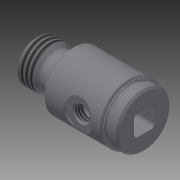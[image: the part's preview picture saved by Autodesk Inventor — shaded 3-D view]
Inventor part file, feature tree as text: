
AUTODESK INVENTOR PART (.ipt)
format: ipt  version: 2013 (Build 170138000, 138)  size: 262,656 bytes
history: native  units: in
note: dims shown in document units (in); Inventor stores cm internally (conversion verified against a paired STEP export)
features: other x119, sketch x5, revolve x4, thread x2, extrude x1
ambient origin geometry x8: Origin, YZ Plane, XZ Plane, XY Plane, X Axis, Y Axis, Z Axis, Center Point
bodies: Solid1 (feature_tree)
feature tree (131):
  revolve  "Revolution1"  [1 undecoded]
  thread  "Thread1"  [1 undecoded]
  revolve  "Revolution2"  [1 undecoded]
  revolve  "Revolution3"  [1 undecoded]
  thread  "Thread2"  [1 undecoded]
  revolve  "Revolution4"  [1 undecoded]
  extrude  "Extrusion1"  [1 undecoded]
  other  "m1_XY"
  other  "m1_YZ"
  other  "m1_ZX"
  other  "m1_X"
  other  "m1_Y"
  other  "m1_Z"
  other  "m1_Center"
  other  "m2_XY"
  other  "m2_YZ"
  other  "m2_ZX"
  other  "m2_X"
  other  "m2_Y"
  other  "m2_Z"
  other  "m2_Center"
  other  "s1_XY"
  other  "s1_YZ"
  other  "s1_ZX"
  other  "s1_X"
  other  "s1_Y"
  other  "s1_Z"
  other  "s1_Center"
  other  "s2_XY"
  other  "s2_YZ"
  other  "s2_ZX"
  other  "s2_X"
  other  "s2_Y"
  other  "s2_Z"
  other  "s2_Center"
  other  "dp1_XY"
  other  "dp1_YZ"
  other  "dp1_ZX"
  other  "dp1_X"
  other  "dp1_Y"
  other  "dp1_Z"
  other  "dp1_Center"
  other  "dp2_XY"
  other  "dp2_YZ"
  other  "dp2_ZX"
  other  "dp2_X"
  other  "dp2_Y"
  other  "dp2_Z"
  other  "dp2_Center"
  other  "rod_guide_XY"
  other  "rod_guide_YZ"
  other  "rod_guide_ZX"
  other  "rod_guide_X"
  other  "rod_guide_Y"
  other  "rod_guide_Z"
  other  "rod_guide_Center"
  other  "to_tube_XY"
  other  "to_tube_YZ"
  other  "to_tube_ZX"
  other  "to_tube_X"
  other  "to_tube_Y"
  other  "to_tube_Z"
  other  "to_tube_Center"
  other  "to_foot_bracket_XY"
  other  "to_foot_bracket_YZ"
  other  "to_foot_bracket_ZX"
  other  "to_foot_bracket_X"
  other  "to_foot_bracket_Y"
  other  "to_foot_bracket_Z"
  other  "to_foot_bracket_Center"
  other  "to_nut_XY"
  other  "to_nut_YZ"
  other  "to_nut_ZX"
  other  "to_nut_X"
  other  "to_nut_Y"
  other  "to_nut_Z"
  other  "to_nut_Center"
  other  "to_trunnion_brackets_XY"
  other  "to_trunnion_brackets_YZ"
  other  "to_trunnion_brackets_ZX"
  other  "to_trunnion_brackets_X"
  other  "to_trunnion_brackets_Y"
  other  "to_trunnion_brackets_Z"
  other  "to_trunnion_brackets_Center"
  other  "to_trunnion_brackets1_XY"
  other  "to_trunnion_brackets1_YZ"
  other  "to_trunnion_brackets1_ZX"
  other  "to_trunnion_brackets1_X"
  other  "to_trunnion_brackets1_Y"
  other  "to_trunnion_brackets1_Z"
  other  "to_trunnion_brackets1_Center"
  other  "to_trunnion_brackets2_XY"
  other  "to_trunnion_brackets2_YZ"
  other  "to_trunnion_brackets2_ZX"
  other  "to_trunnion_brackets2_X"
  other  "to_trunnion_brackets2_Y"
  other  "to_trunnion_brackets2_Z"
  other  "to_trunnion_brackets2_Center"
  other  "t1_XY"
  other  "t1_YZ"
  other  "t1_ZX"
  other  "t1_X"
  other  "t1_Y"
  other  "t1_Z"
  other  "t1_Center"
  other  "port_XY"
  other  "port_YZ"
  other  "port_ZX"
  other  "port_X"
  other  "port_Y"
  other  "port_Z"
  other  "port_Center"
  other  "rod_guide_1_XY"
  other  "rod_guide_1_YZ"
  other  "rod_guide_1_ZX"
  other  "rod_guide_1_X"
  other  "rod_guide_1_Y"
  other  "rod_guide_1_Z"
  other  "rod_guide_1_Center"
  other  "rod_guide_11_XY"
  other  "rod_guide_11_YZ"
  other  "rod_guide_11_ZX"
  other  "rod_guide_11_X"
  other  "rod_guide_11_Y"
  other  "rod_guide_11_Z"
  other  "rod_guide_11_Center"
  sketch  "Sketch_2"  dims[d0=360.0deg d1=0.1537in d2=0.0in d3=360.0deg]
  sketch  "Sketch_3"  dims[d4=360.0deg d5=0.0955in d6=0.212in]
  sketch  "Sketch_12"  dims[d7=360.0deg d8=2.312in d9=0.0in]
  sketch  "Sketch_47"
  sketch  "Sketch_33"
note: 7 required parameter values undecoded (feature->parameter linkage not recoverable at this tier; creation-order binding heuristic only, values carry confidence <= 0.55)